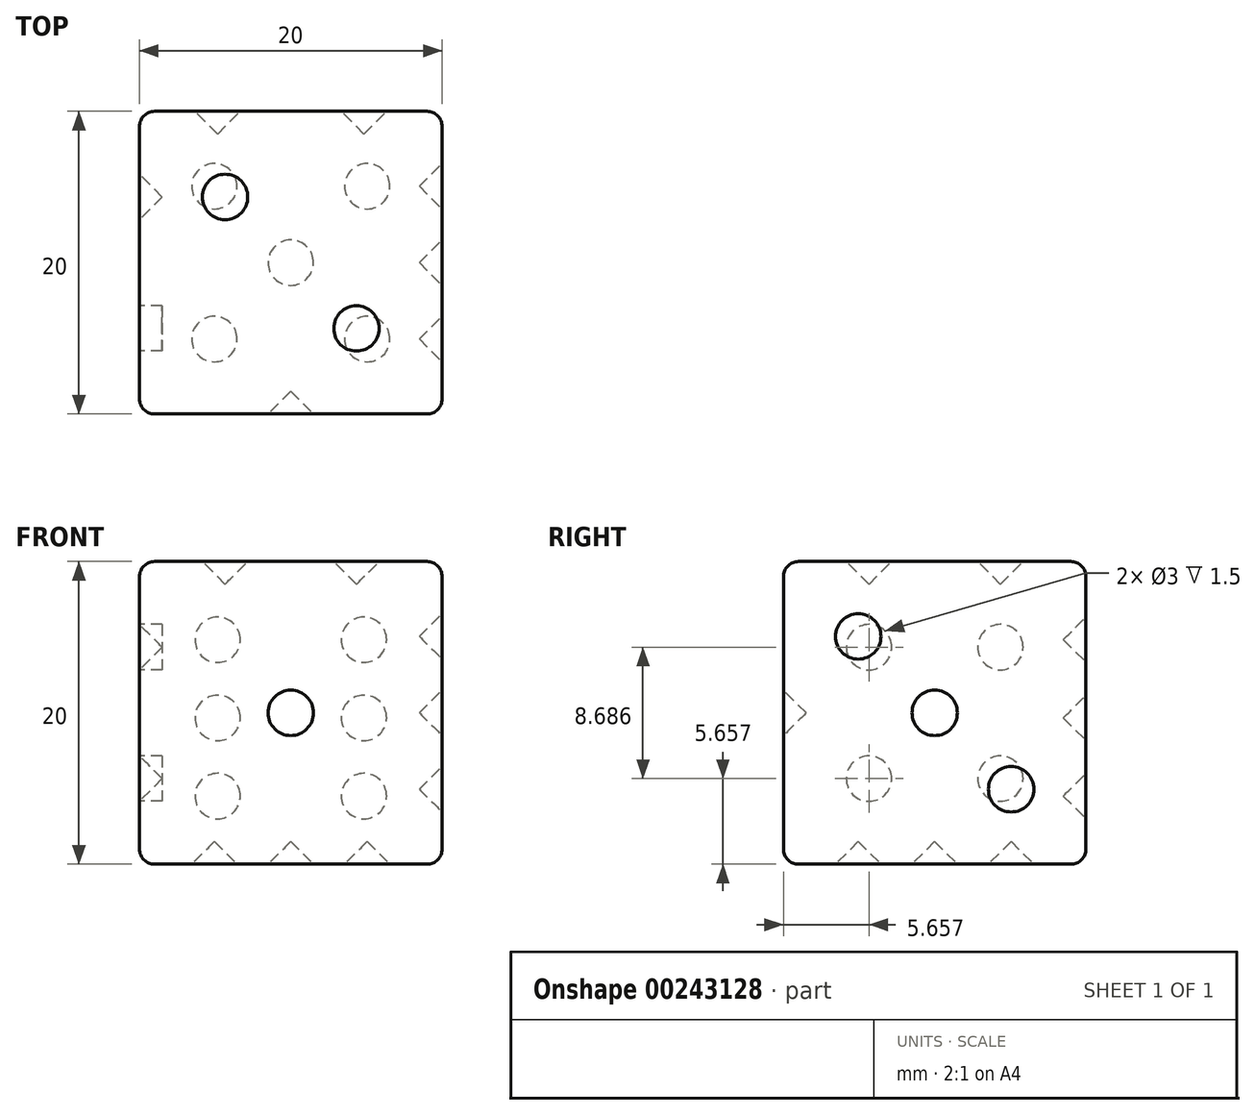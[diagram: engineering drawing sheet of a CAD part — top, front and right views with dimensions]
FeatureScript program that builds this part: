
annotation { "Feature Type Name" : "Feature", "Feature Type Description" : "" }
export const myFeature = defineFeature(function(context is Context, id is Id, definition is map)
    precondition{}
    {
        {
            var Q0;
            Q0=qCreatedBy(makeId("Top.planeOp"),FACE);
            var sketch = newSketch(context, id + "F0", { "sketchPlane" : qUnion([Q0])});
            skLineSegment(sketch, "E0.bottom", {"start": v(0, 0) * mm, "end": v(20, 0) * mm});
            skLineSegment(sketch, "E0.top", {"start": v(0, 20) * mm, "end": v(20, 20) * mm});
            skLineSegment(sketch, "E0.left", {"start": v(0, 0) * mm, "end": v(0, 20) * mm});
            skLineSegment(sketch, "E0.right", {"start": v(20, 0) * mm, "end": v(20, 20) * mm});
            skSolve(sketch);
        }
        {
            var Q0;
            Q0 = qSketchRegion(id + "F0", true);
            extrude(context, id + "F1", {"entities" : qUnion([Q0]), "depth" : 20 * mm});
        }
        {
            var Q0;
            Q0=makeQuery(id+"F1.opExtrude","SWEPT_FACE",FACE,{"disambiguationData":[OSD([sQuery(id+"F0.wireOp",EDGE,"E0.bottom")])]});
            var sketch = newSketch(context, id + "F2", { "sketchPlane" : qUnion([Q0])});
            skLineSegment(sketch, "E1", {"start": v(10, 20) * mm, "end": v(10, 0) * mm, "construction": true});
            skCircle(sketch, "E2", {"center": v(10, 10) * mm, "radius": 1.5 * mm});
            skSolve(sketch);
        }
        {
            var Q0;
            Q0=makeQuery(id+"F2.imprint","IMPRINT",FACE,{"disambiguationData":[TD([[makeQuery(id+"F2.imprint","IMPRINT",EDGE,{"derivedFrom":sQuery(id+"F2.wireOp",EDGE,"E2")}),1.0]])]});
            extrude(context, id + "F3", {"entities" : qUnion([Q0]), "operationType" : NewBodyOperationType.REMOVE, "oppositeDirection" : true, "depth" : 1.5 * mm});
        }
        {
            var Q0;
            Q0=makeQuery(id+"F1.opExtrude","CAP_FACE",FACE,{"disambiguationData":[OSD([sQuery(id+"F0.wireOp",EDGE,"E0.bottom"),sQuery(id+"F0.wireOp",EDGE,"E0.top"),sQuery(id+"F0.wireOp",EDGE,"E0.left"),sQuery(id+"F0.wireOp",EDGE,"E0.right")])],"isStart":false});
            var sketch = newSketch(context, id + "F4", { "sketchPlane" : qUnion([Q0])});
            skLineSegment(sketch, "E3", {"start": v(0, 20) * mm, "end": v(5.66, 14.34) * mm, "construction": true});
            skLineSegment(sketch, "E4", {"start": v(20, 0) * mm, "end": v(14.34, 5.66) * mm, "construction": true});
            skCircle(sketch, "E5", {"center": v(5.66, 14.34) * mm, "radius": 1.5 * mm});
            skCircle(sketch, "E6", {"center": v(14.34, 5.66) * mm, "radius": 1.5 * mm});
            skSolve(sketch);
        }
        {
            var Q0;
            Q0=makeQuery(id+"F4.imprint","IMPRINT",FACE,{"disambiguationData":[TD([[makeQuery(id+"F4.imprint","IMPRINT",EDGE,{"derivedFrom":sQuery(id+"F4.wireOp",EDGE,"E6")}),1.0]])]});
            var Q1;
            Q1=makeQuery(id+"F4.imprint","IMPRINT",FACE,{"disambiguationData":[TD([[makeQuery(id+"F4.imprint","IMPRINT",EDGE,{"derivedFrom":sQuery(id+"F4.wireOp",EDGE,"E5")}),1.0]])]});
            extrude(context, id + "F5", {"entities" : qUnion([Q0, Q1]), "operationType" : NewBodyOperationType.REMOVE, "oppositeDirection" : true, "depth" : 1.5 * mm});
        }
        {
            var Q0;
            Q0=makeQuery(id+"F1.opExtrude","CAP_EDGE",EDGE,{"disambiguationData":[OSD([sQuery(id+"F0.wireOp",EDGE,"E0.left")])],"isStart":false});
            var Q1;
            Q1=makeQuery(id+"F1.opExtrude","CAP_EDGE",EDGE,{"disambiguationData":[OSD([sQuery(id+"F0.wireOp",EDGE,"E0.top")])],"isStart":false});
            var Q2;
            Q2=makeQuery(id+"F1.opExtrude","CAP_EDGE",EDGE,{"disambiguationData":[OSD([sQuery(id+"F0.wireOp",EDGE,"E0.right")])],"isStart":false});
            var Q3;
            Q3=makeQuery(id+"F1.opExtrude","CAP_EDGE",EDGE,{"disambiguationData":[OSD([sQuery(id+"F0.wireOp",EDGE,"E0.right")])],"isStart":true});
            var Q4;
            Q4=makeQuery(id+"F1.opExtrude","CAP_EDGE",EDGE,{"disambiguationData":[OSD([sQuery(id+"F0.wireOp",EDGE,"E0.bottom")])],"isStart":false});
            var Q5;
            Q5=makeQuery(id+"F1.opExtrude","CAP_EDGE",EDGE,{"disambiguationData":[OSD([sQuery(id+"F0.wireOp",EDGE,"E0.bottom")])],"isStart":true});
            var Q6;
            Q6=makeQuery(id+"F1.opExtrude","SWEPT_EDGE",EDGE,{"disambiguationData":[OSD([sQuery(id+"F0.wireOp",EDGE,"E0.bottom"),sQuery(id+"F0.wireOp",EDGE,"E0.left")])]});
            var Q7;
            Q7=makeQuery(id+"F1.opExtrude","SWEPT_EDGE",EDGE,{"disambiguationData":[OSD([sQuery(id+"F0.wireOp",EDGE,"E0.bottom"),sQuery(id+"F0.wireOp",EDGE,"E0.right")])]});
            var Q8;
            Q8=makeQuery(id+"F1.opExtrude","SWEPT_EDGE",EDGE,{"disambiguationData":[OSD([sQuery(id+"F0.wireOp",EDGE,"E0.top"),sQuery(id+"F0.wireOp",EDGE,"E0.right")])]});
            var Q9;
            Q9=makeQuery(id+"F1.opExtrude","CAP_EDGE",EDGE,{"disambiguationData":[OSD([sQuery(id+"F0.wireOp",EDGE,"E0.top")])],"isStart":true});
            var Q10;
            Q10=makeQuery(id+"F1.opExtrude","CAP_EDGE",EDGE,{"disambiguationData":[OSD([sQuery(id+"F0.wireOp",EDGE,"E0.left")])],"isStart":true});
            var Q11;
            Q11=makeQuery(id+"F1.opExtrude","SWEPT_EDGE",EDGE,{"disambiguationData":[OSD([sQuery(id+"F0.wireOp",EDGE,"E0.top"),sQuery(id+"F0.wireOp",EDGE,"E0.left")])]});
            fillet(context, id + "F6", {"entities" : qUnion([Q0, Q1, Q2, Q3, Q4, Q5, Q6, Q7, Q8, Q9, Q10, Q11]), "radius" : 1 * mm, "tangentPropagation" : true, "allowEdgeOverflow" : false});
        }
        {
            var Q0;
            Q0=makeQuery(id+"F5.boolean.opBoolean","COPY",EDGE,{"derivedFrom":makeQuery(id+"F5.opExtrude","CAP_EDGE",EDGE,{"disambiguationData":[OSD([sQuery(id+"F4.wireOp",EDGE,"E6")])],"isStart":false})});
            var Q1;
            Q1=makeQuery(id+"F5.boolean.opBoolean","COPY",EDGE,{"derivedFrom":makeQuery(id+"F5.opExtrude","CAP_EDGE",EDGE,{"disambiguationData":[OSD([sQuery(id+"F4.wireOp",EDGE,"E5")])],"isStart":false})});
            var Q2;
            Q2=makeQuery(id+"F3.boolean.opBoolean","COPY",EDGE,{"derivedFrom":makeQuery(id+"F3.opExtrude","CAP_EDGE",EDGE,{"disambiguationData":[OSD([sQuery(id+"F2.wireOp",EDGE,"E2")])],"isStart":false})});
            chamfer(context, id + "F7", {"entities" : qUnion([Q0, Q1, Q2]), "width" : 1.5 * mm, "tangentPropagation" : true});
        }
        {
            var Q0;
            Q0=makeQuery(id+"F1.opExtrude","SWEPT_FACE",FACE,{"disambiguationData":[OSD([sQuery(id+"F0.wireOp",EDGE,"E0.right")])]});
            var sketch = newSketch(context, id + "F8", { "sketchPlane" : qUnion([Q0])});
            skCircle(sketch, "E7", {"center": v(15.05, 4.95) * mm, "radius": 1.5 * mm});
            skCircle(sketch, "E8", {"center": v(4.95, 15.05) * mm, "radius": 1.5 * mm});
            skCircle(sketch, "E9", {"center": v(10, 10) * mm, "radius": 1.5 * mm});
            skSolve(sketch);
        }
        {
            var Q0;
            Q0 = qSketchRegion(id + "F8", true);
            extrude(context, id + "F9", {"entities" : qUnion([Q0]), "operationType" : NewBodyOperationType.REMOVE, "oppositeDirection" : true, "depth" : 1.5 * mm});
        }
        {
            var Q0;
            Q0=makeQuery(id+"F9.boolean.opBoolean","COPY",FACE,{"derivedFrom":makeQuery(id+"F9.opExtrude","CAP_FACE",FACE,{"disambiguationData":[OSD([sQuery(id+"F8.wireOp",EDGE,"E8")])],"isStart":false})});
            var Q1;
            Q1=makeQuery(id+"F9.boolean.opBoolean","COPY",FACE,{"derivedFrom":makeQuery(id+"F9.opExtrude","CAP_FACE",FACE,{"disambiguationData":[OSD([sQuery(id+"F8.wireOp",EDGE,"E9")])],"isStart":false})});
            var Q2;
            Q2=makeQuery(id+"F9.boolean.opBoolean","COPY",FACE,{"derivedFrom":makeQuery(id+"F9.opExtrude","CAP_FACE",FACE,{"disambiguationData":[OSD([sQuery(id+"F8.wireOp",EDGE,"E7")])],"isStart":false})});
            chamfer(context, id + "F10", {"entities" : qUnion([Q0, Q1, Q2]), "width" : 1.5 * mm, "tangentPropagation" : true});
        }
        {
            var Q0;
            Q0=makeQuery(id+"F1.opExtrude","SWEPT_FACE",FACE,{"disambiguationData":[OSD([sQuery(id+"F0.wireOp",EDGE,"E0.left")])]});
            var sketch = newSketch(context, id + "F11", { "sketchPlane" : qUnion([Q0])});
            skLineSegment(sketch, "E10", {"start": v(-20, 20) * mm, "end": v(-14.34, 14.34) * mm, "construction": true});
            skLineSegment(sketch, "E11", {"start": v(-20, 0) * mm, "end": v(-14.34, 5.66) * mm, "construction": true});
            skCircle(sketch, "E12", {"center": v(-14.34, 14.34) * mm, "radius": 1.5 * mm});
            skCircle(sketch, "E13", {"center": v(-14.34, 5.66) * mm, "radius": 1.5 * mm});
            skLineSegment(sketch, "E14", {"start": v(-10, 20) * mm, "end": v(-10, 0) * mm, "construction": true});
            skCircle(sketch, "E15.MirrorC", {"center": v(-5.66, 14.34) * mm, "radius": 1.5 * mm});
            skCircle(sketch, "E16.MirrorC", {"center": v(-5.66, 5.66) * mm, "radius": 1.5 * mm});
            skSolve(sketch);
        }
        {
            var Q0;
            Q0 = qSketchRegion(id + "F11", true);
            extrude(context, id + "F12", {"entities" : qUnion([Q0]), "operationType" : NewBodyOperationType.REMOVE, "oppositeDirection" : true, "depth" : 1.5 * mm});
        }
        {
            var Q0;
            Q0=makeQuery(id+"F12.boolean.opBoolean","COPY",EDGE,{"derivedFrom":makeQuery(id+"F12.opExtrude","CAP_EDGE",EDGE,{"disambiguationData":[OSD([sQuery(id+"F11.wireOp",EDGE,"E12")])],"isStart":false})});
            var Q1;
            Q1=makeQuery(id+"F12.boolean.opBoolean","COPY",EDGE,{"derivedFrom":makeQuery(id+"F12.opExtrude","CAP_EDGE",EDGE,{"disambiguationData":[OSD([sQuery(id+"F11.wireOp",EDGE,"E13")])],"isStart":false})});
            chamfer(context, id + "F13", {"entities" : qUnion([Q0, Q1]), "width" : 1.5 * mm, "tangentPropagation" : true});
        }
        {
            var Q0;
            Q0=makeQuery(id+"F1.opExtrude","CAP_FACE",FACE,{"disambiguationData":[OSD([sQuery(id+"F0.wireOp",EDGE,"E0.bottom"),sQuery(id+"F0.wireOp",EDGE,"E0.top"),sQuery(id+"F0.wireOp",EDGE,"E0.left"),sQuery(id+"F0.wireOp",EDGE,"E0.right")])],"isStart":true});
            var sketch = newSketch(context, id + "F14", { "sketchPlane" : qUnion([Q0])});
            skLineSegment(sketch, "E17", {"start": v(0, 0) * mm, "end": v(4.95, -4.95) * mm, "construction": true});
            skLineSegment(sketch, "E18", {"start": v(20, -20) * mm, "end": v(15.05, -15.05) * mm, "construction": true});
            skLineSegment(sketch, "E19", {"start": v(20, 0) * mm, "end": v(15.05, -4.95) * mm, "construction": true});
            skLineSegment(sketch, "E20", {"start": v(0, -20) * mm, "end": v(4.95, -15.05) * mm, "construction": true});
            skCircle(sketch, "E21", {"center": v(4.95, -15.05) * mm, "radius": 1.5 * mm});
            skCircle(sketch, "E22", {"center": v(15.05, -15.05) * mm, "radius": 1.5 * mm});
            skCircle(sketch, "E23", {"center": v(15.05, -4.95) * mm, "radius": 1.5 * mm});
            skCircle(sketch, "E24", {"center": v(4.95, -4.95) * mm, "radius": 1.5 * mm});
            skCircle(sketch, "E25", {"center": v(10, -10) * mm, "radius": 1.5 * mm});
            skSolve(sketch);
        }
        {
            var Q0;
            Q0 = qSketchRegion(id + "F14", true);
            extrude(context, id + "F15", {"entities" : qUnion([Q0]), "operationType" : NewBodyOperationType.REMOVE, "oppositeDirection" : true, "depth" : 1.5 * mm});
        }
        {
            var Q0;
            Q0=makeQuery(id+"F15.boolean.opBoolean","COPY",EDGE,{"derivedFrom":makeQuery(id+"F15.opExtrude","CAP_EDGE",EDGE,{"disambiguationData":[OSD([sQuery(id+"F14.wireOp",EDGE,"E24")])],"isStart":false})});
            var Q1;
            Q1=makeQuery(id+"F15.boolean.opBoolean","COPY",EDGE,{"derivedFrom":makeQuery(id+"F15.opExtrude","CAP_EDGE",EDGE,{"disambiguationData":[OSD([sQuery(id+"F14.wireOp",EDGE,"E23")])],"isStart":false})});
            var Q2;
            Q2=makeQuery(id+"F15.boolean.opBoolean","COPY",EDGE,{"derivedFrom":makeQuery(id+"F15.opExtrude","CAP_EDGE",EDGE,{"disambiguationData":[OSD([sQuery(id+"F14.wireOp",EDGE,"E25")])],"isStart":false})});
            var Q3;
            Q3=makeQuery(id+"F15.boolean.opBoolean","COPY",EDGE,{"derivedFrom":makeQuery(id+"F15.opExtrude","CAP_EDGE",EDGE,{"disambiguationData":[OSD([sQuery(id+"F14.wireOp",EDGE,"E21")])],"isStart":false})});
            var Q4;
            Q4=makeQuery(id+"F15.boolean.opBoolean","COPY",EDGE,{"derivedFrom":makeQuery(id+"F15.opExtrude","CAP_EDGE",EDGE,{"disambiguationData":[OSD([sQuery(id+"F14.wireOp",EDGE,"E22")])],"isStart":false})});
            chamfer(context, id + "F16", {"entities" : qUnion([Q0, Q1, Q2, Q3, Q4]), "width" : 1.5 * mm, "tangentPropagation" : true});
        }
        {
            var Q0;
            Q0=makeQuery(id+"F1.opExtrude","SWEPT_FACE",FACE,{"disambiguationData":[OSD([sQuery(id+"F0.wireOp",EDGE,"E0.top")])]});
            var sketch = newSketch(context, id + "F17", { "sketchPlane" : qUnion([Q0])});
            skLineSegment(sketch, "E26", {"start": v(-20, 20) * mm, "end": v(-14.83, 20) * mm, "construction": true});
            skLineSegment(sketch, "E27", {"start": v(0, 20) * mm, "end": v(-5.17, 20) * mm, "construction": true});
            skLineSegment(sketch, "E28", {"start": v(-14.83, 20) * mm, "end": v(-14.83, 14.83) * mm, "construction": true});
            skLineSegment(sketch, "E29", {"start": v(-14.83, 14.83) * mm, "end": v(-14.83, 9.67) * mm, "construction": true});
            skLineSegment(sketch, "E30", {"start": v(-5.17, 20) * mm, "end": v(-5.17, 14.83) * mm, "construction": true});
            skLineSegment(sketch, "E31", {"start": v(-5.17, 14.83) * mm, "end": v(-5.17, 9.67) * mm, "construction": true});
            skCircle(sketch, "E32", {"center": v(-5.17, 9.67) * mm, "radius": 1.5 * mm});
            skCircle(sketch, "E33", {"center": v(-5.17, 14.83) * mm, "radius": 1.5 * mm});
            skLineSegment(sketch, "E34", {"start": v(-14.83, 9.67) * mm, "end": v(-14.83, 4.5) * mm, "construction": true});
            skLineSegment(sketch, "E35", {"start": v(-5.17, 9.67) * mm, "end": v(-5.17, 4.5) * mm, "construction": true});
            skCircle(sketch, "E36", {"center": v(-14.83, 4.5) * mm, "radius": 1.5 * mm});
            skCircle(sketch, "E37", {"center": v(-5.17, 4.5) * mm, "radius": 1.5 * mm});
            skCircle(sketch, "E38", {"center": v(-14.83, 14.83) * mm, "radius": 1.5 * mm});
            skCircle(sketch, "E39", {"center": v(-14.83, 9.67) * mm, "radius": 1.5 * mm});
            skSolve(sketch);
        }
        {
            var Q0;
            Q0 = qSketchRegion(id + "F17", true);
            extrude(context, id + "F18", {"entities" : qUnion([Q0]), "operationType" : NewBodyOperationType.REMOVE, "oppositeDirection" : true, "depth" : 1.5 * mm});
        }
        {
            var Q0;
            Q0=makeQuery(id+"F18.boolean.opBoolean","COPY",EDGE,{"derivedFrom":makeQuery(id+"F18.opExtrude","CAP_EDGE",EDGE,{"disambiguationData":[OSD([sQuery(id+"F17.wireOp",EDGE,"E38")])],"isStart":false})});
            var Q1;
            Q1=makeQuery(id+"F18.boolean.opBoolean","COPY",EDGE,{"derivedFrom":makeQuery(id+"F18.opExtrude","CAP_EDGE",EDGE,{"disambiguationData":[OSD([sQuery(id+"F17.wireOp",EDGE,"E33")])],"isStart":false})});
            var Q2;
            Q2=makeQuery(id+"F18.boolean.opBoolean","COPY",EDGE,{"derivedFrom":makeQuery(id+"F18.opExtrude","CAP_EDGE",EDGE,{"disambiguationData":[OSD([sQuery(id+"F17.wireOp",EDGE,"E32")])],"isStart":false})});
            var Q3;
            Q3=makeQuery(id+"F18.boolean.opBoolean","COPY",EDGE,{"derivedFrom":makeQuery(id+"F18.opExtrude","CAP_EDGE",EDGE,{"disambiguationData":[OSD([sQuery(id+"F17.wireOp",EDGE,"E37")])],"isStart":false})});
            var Q4;
            Q4=makeQuery(id+"F18.boolean.opBoolean","COPY",EDGE,{"derivedFrom":makeQuery(id+"F18.opExtrude","CAP_EDGE",EDGE,{"disambiguationData":[OSD([sQuery(id+"F17.wireOp",EDGE,"E36")])],"isStart":false})});
            var Q5;
            Q5=makeQuery(id+"F18.boolean.opBoolean","COPY",EDGE,{"derivedFrom":makeQuery(id+"F18.opExtrude","CAP_EDGE",EDGE,{"disambiguationData":[OSD([sQuery(id+"F17.wireOp",EDGE,"E39")])],"isStart":false})});
            chamfer(context, id + "F19", {"entities" : qUnion([Q0, Q1, Q2, Q3, Q4, Q5]), "width" : 1.5 * mm, "tangentPropagation" : true});
        }
    });
